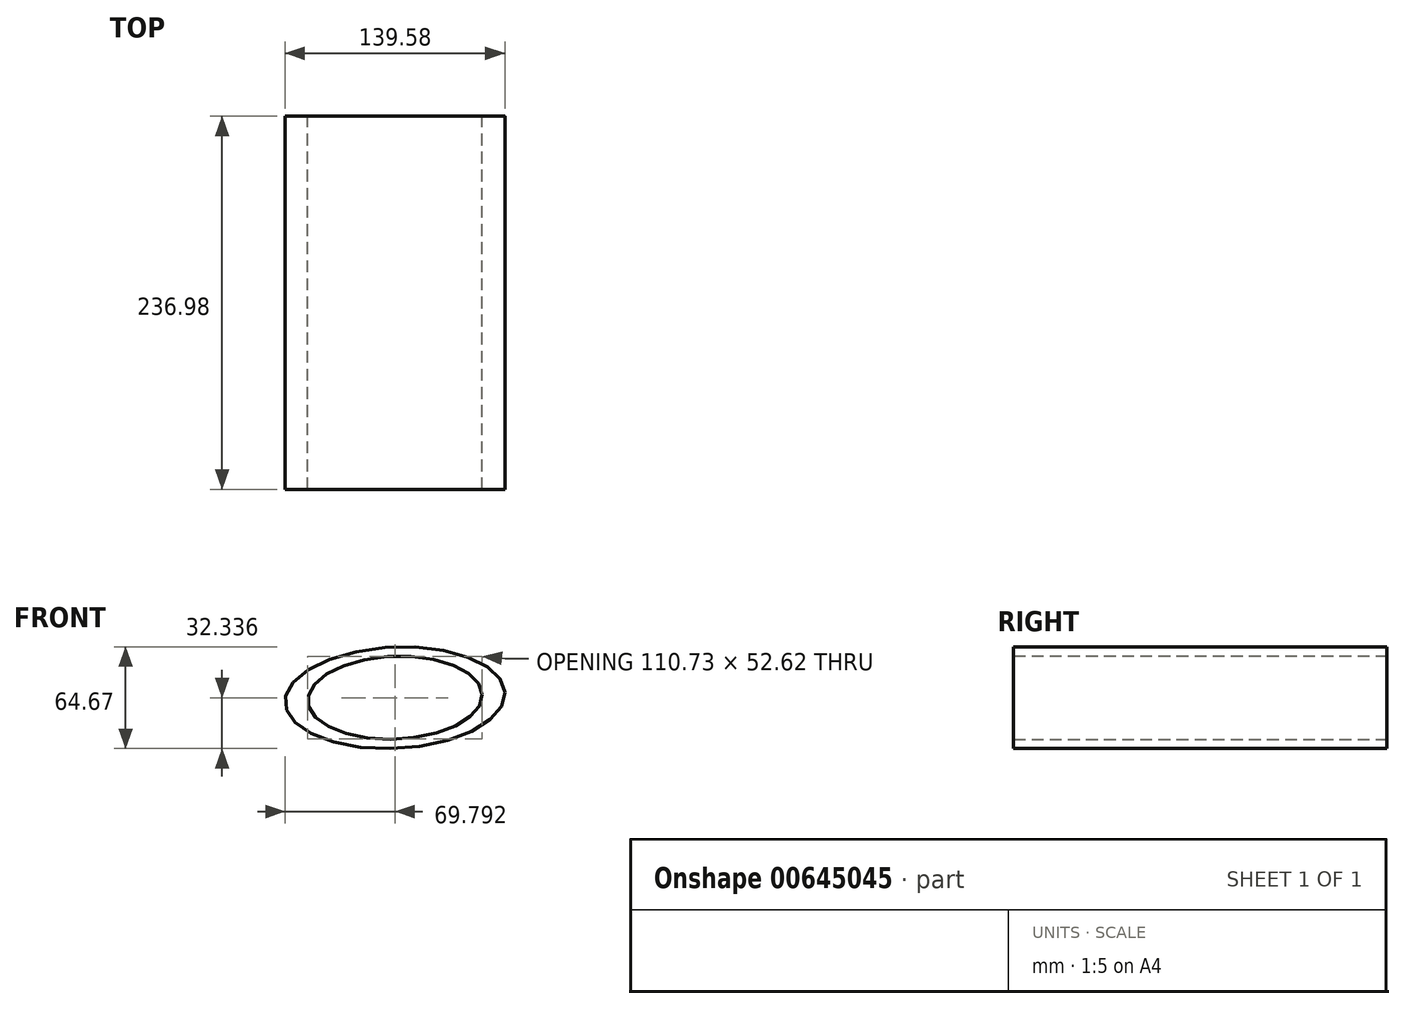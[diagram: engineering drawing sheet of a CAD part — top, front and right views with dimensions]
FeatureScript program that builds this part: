
annotation { "Feature Type Name" : "Feature", "Feature Type Description" : "" }
export const myFeature = defineFeature(function(context is Context, id is Id, definition is map)
    precondition{}
    {
        {
            var Q0;
            Q0=qCreatedBy(makeId("Front.planeOp"),FACE);
            var sketch = newSketch(context, id + "F0", { "sketchPlane" : qUnion([Q0])});
            skEllipse(sketch, "E0", {"center": v(-10.12, 4.54) * mm, "majorRadius": 69.85 * mm, "minorRadius": 32.2 * mm, "majorAxis": v(1, 0.05)});
            skSolve(sketch);
        }
        {
            var Q0;
            Q0 = qSketchRegion(id + "F0", true);
            extrude(context, id + "F1", {"entities" : qUnion([Q0]), "depth" : 236.98 * mm, "offsetDistance" : 25.4 * mm});
        }
        {
            var Q0;
            Q0=makeQuery(id+"F1.opExtrude","CAP_FACE",FACE,{"disambiguationData":[OSD([sQuery(id+"F0.wireOp",EDGE,"E0")])],"isStart":false});
            var sketch = newSketch(context, id + "F2", { "sketchPlane" : qUnion([Q0])});
            skEllipse(sketch, "E1", {"center": v(-10.12, 4.54) * mm, "majorRadius": 55.4 * mm, "minorRadius": 26.33 * mm, "majorAxis": v(1, 0.04)});
            skSolve(sketch);
        }
        {
            var Q0;
            Q0 = qSketchRegion(id + "F2", true);
            extrude(context, id + "F3", {"entities" : qUnion([Q0]), "operationType" : NewBodyOperationType.REMOVE, "oppositeDirection" : true, "depth" : 238.76 * mm, "offsetDistance" : 25.4 * mm});
        }
    });
